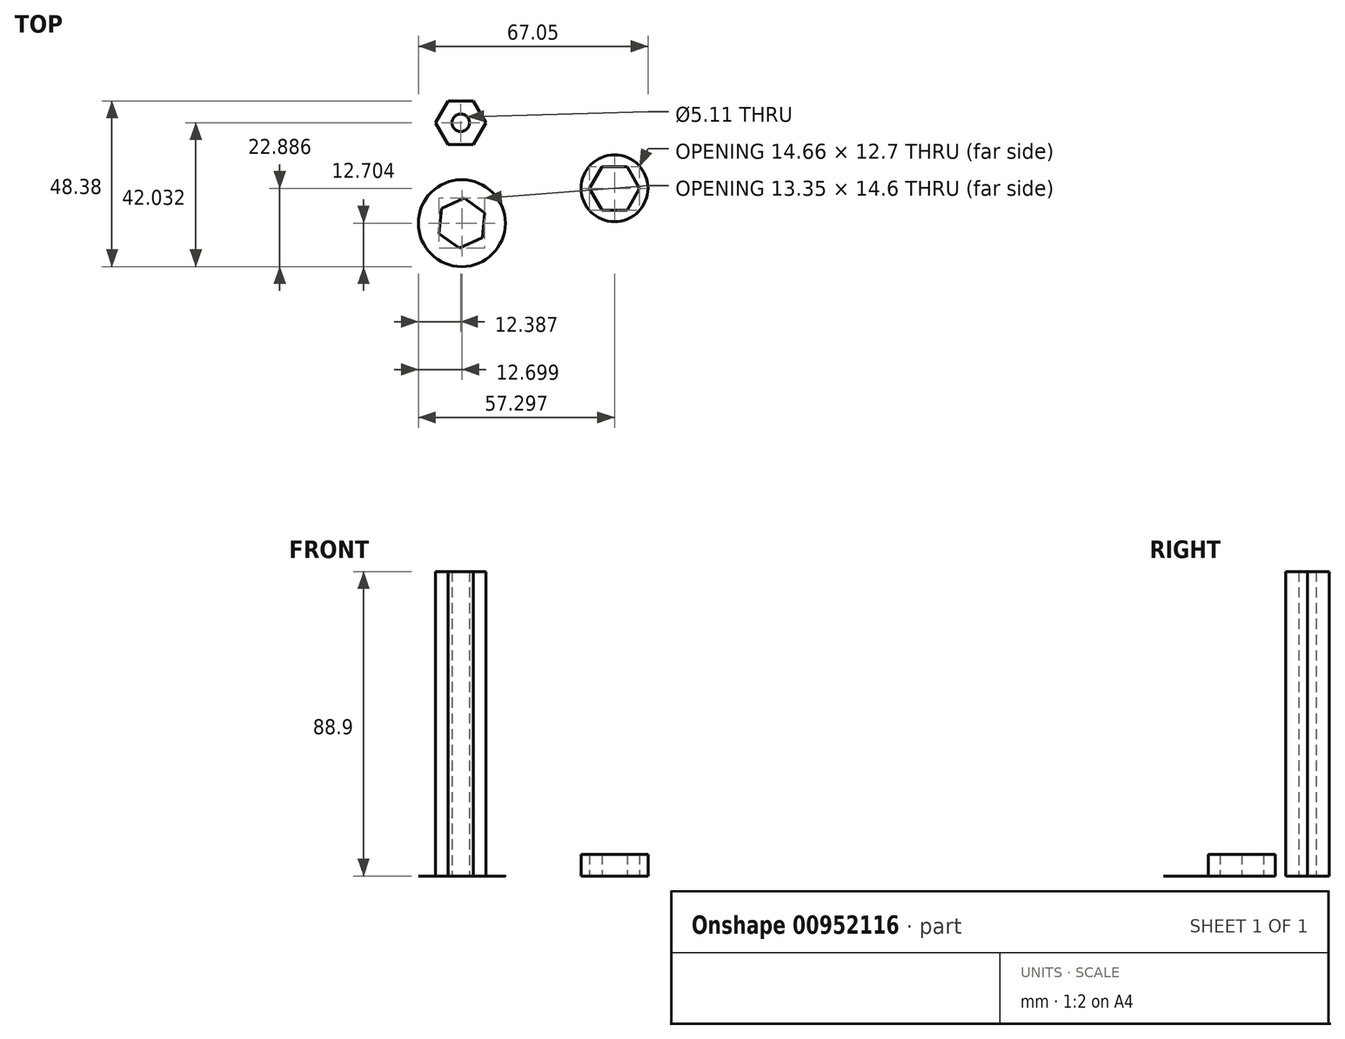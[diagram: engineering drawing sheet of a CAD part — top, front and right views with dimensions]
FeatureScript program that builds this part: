
annotation { "Feature Type Name" : "Feature", "Feature Type Description" : "" }
export const myFeature = defineFeature(function(context is Context, id is Id, definition is map)
    precondition{}
    {
        {
            var Q0;
            Q0=qCreatedBy(makeId("Top.planeOp"),FACE);
            var sketch = newSketch(context, id + "F0", { "sketchPlane" : qUnion([Q0])});
            skCircle(sketch, "E0", {"center": v(-61.71, 37.07) * mm, "radius": 2.55 * mm});
            skCircle(sketch, "E1.cCircle", {"center": v(-61.71, 37.07) * mm, "radius": 6.35 * mm, "construction": true});
            skLineSegment(sketch, "E1.0", {"start": v(-58.05, 30.72) * mm, "end": v(-65.38, 30.72) * mm});
            skLineSegment(sketch, "E1.1", {"start": v(-65.38, 30.72) * mm, "end": v(-69.04, 37.07) * mm});
            skLineSegment(sketch, "E1.2", {"start": v(-69.04, 37.07) * mm, "end": v(-65.38, 43.42) * mm});
            skLineSegment(sketch, "E1.3", {"start": v(-65.38, 43.42) * mm, "end": v(-58.05, 43.42) * mm});
            skLineSegment(sketch, "E1.4", {"start": v(-58.05, 43.42) * mm, "end": v(-54.38, 37.07) * mm});
            skLineSegment(sketch, "E1.5", {"start": v(-54.38, 37.07) * mm, "end": v(-58.05, 30.72) * mm});
            skPoint(sketch, "E1.0.midPoint", {"position": v(-61.71, 30.72) * mm});
            skSolve(sketch);
        }
        {
            var Q0;
            Q0=makeQuery(id+"F0.imprint","IMPRINT",FACE,{"disambiguationData":[TD([[makeQuery(id+"F0.imprint","IMPRINT",EDGE,{"derivedFrom":sQuery(id+"F0.wireOp",EDGE,"E0")}),-1.0]])]});
            extrude(context, id + "F1", {"entities" : qUnion([Q0]), "depth" : 88.9 * mm, "offsetDistance" : 25.4 * mm});
        }
        {
            var Q0;
            Q0=qCreatedBy(makeId("Top.planeOp"),FACE);
            var sketch = newSketch(context, id + "F2", { "sketchPlane" : qUnion([Q0])});
            skCircle(sketch, "E2", {"center": v(-61.4, 7.74) * mm, "radius": 12.7 * mm});
            skCircle(sketch, "E3.cCircle", {"center": v(-61.4, 7.74) * mm, "radius": 6.35 * mm, "construction": true});
            skLineSegment(sketch, "E3.0", {"start": v(-55.44, 3.48) * mm, "end": v(-62.11, 0.45) * mm});
            skLineSegment(sketch, "E3.1", {"start": v(-62.11, 0.45) * mm, "end": v(-68.08, 4.7) * mm});
            skLineSegment(sketch, "E3.2", {"start": v(-68.08, 4.7) * mm, "end": v(-67.37, 12) * mm});
            skLineSegment(sketch, "E3.3", {"start": v(-67.37, 12) * mm, "end": v(-60.7, 15.04) * mm});
            skLineSegment(sketch, "E3.4", {"start": v(-60.7, 15.04) * mm, "end": v(-54.73, 10.78) * mm});
            skLineSegment(sketch, "E3.5", {"start": v(-54.73, 10.78) * mm, "end": v(-55.44, 3.48) * mm});
            skPoint(sketch, "E3.0.midPoint", {"position": v(-58.77, 1.96) * mm});
            skSolve(sketch);
        }
        {
            var Q0;
            Q0 = qSketchRegion(id + "F2", true);
            extrude(context, id + "F3", {"entities" : qUnion([Q0]), "depth" : 1 / 203.2 * mm, "offsetDistance" : 25.4 * mm});
        }
        {
            var Q0;
            Q0=qCreatedBy(makeId("Top.planeOp"),FACE);
            var sketch = newSketch(context, id + "F4", { "sketchPlane" : qUnion([Q0])});
            skCircle(sketch, "E4", {"center": v(-16.8, 17.93) * mm, "radius": 9.75 * mm});
            skCircle(sketch, "E5.cCircle", {"center": v(-16.8, 17.93) * mm, "radius": 6.35 * mm, "construction": true});
            skLineSegment(sketch, "E5.0", {"start": v(-13.14, 11.58) * mm, "end": v(-20.47, 11.58) * mm});
            skLineSegment(sketch, "E5.1", {"start": v(-20.47, 11.58) * mm, "end": v(-24.13, 17.93) * mm});
            skLineSegment(sketch, "E5.2", {"start": v(-24.13, 17.93) * mm, "end": v(-20.47, 24.28) * mm});
            skLineSegment(sketch, "E5.3", {"start": v(-20.47, 24.28) * mm, "end": v(-13.14, 24.28) * mm});
            skLineSegment(sketch, "E5.4", {"start": v(-13.14, 24.28) * mm, "end": v(-9.47, 17.93) * mm});
            skLineSegment(sketch, "E5.5", {"start": v(-9.47, 17.93) * mm, "end": v(-13.14, 11.58) * mm});
            skPoint(sketch, "E5.0.midPoint", {"position": v(-16.8, 11.58) * mm});
            skSolve(sketch);
        }
        {
            var Q0;
            Q0=makeQuery(id+"F4.imprint","IMPRINT",FACE,{"disambiguationData":[TD([[makeQuery(id+"F4.imprint","IMPRINT",EDGE,{"derivedFrom":sQuery(id+"F4.wireOp",EDGE,"E4")}),1.0]])]});
            extrude(context, id + "F5", {"entities" : qUnion([Q0]), "depth" : 6.35 * mm, "offsetDistance" : 25.4 * mm});
        }
    });
